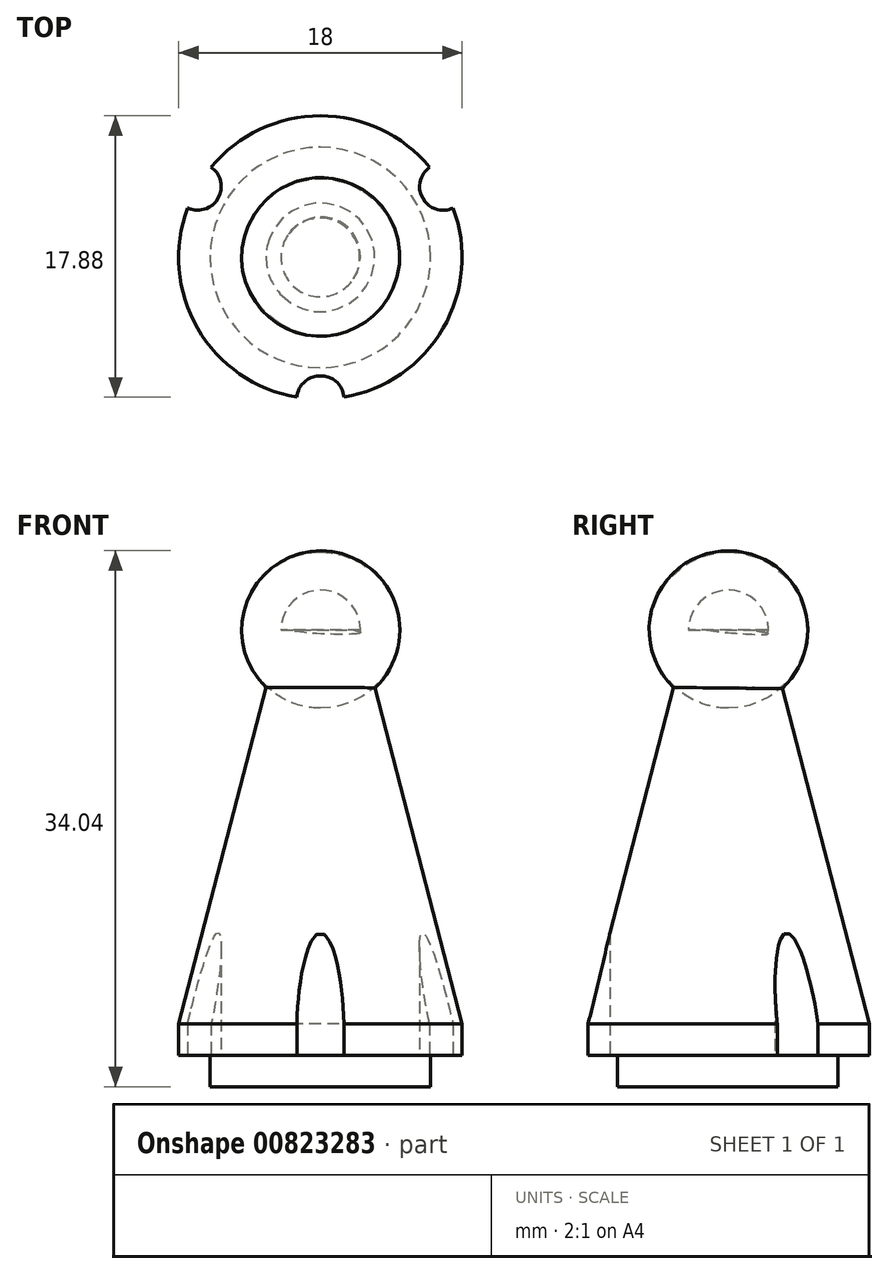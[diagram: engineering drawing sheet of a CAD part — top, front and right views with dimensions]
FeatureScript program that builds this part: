
annotation { "Feature Type Name" : "Feature", "Feature Type Description" : "" }
export const myFeature = defineFeature(function(context is Context, id is Id, definition is map)
    precondition{}
    {
        {
            var Q0;
            Q0=qCreatedBy(makeId("Top.planeOp"),FACE);
            var sketch = newSketch(context, id + "F0", { "sketchPlane" : qUnion([Q0])});
            skCircle(sketch, "E0", {"center": v(0, 0) * mm, "radius": 7 * mm});
            skSolve(sketch);
        }
        {
            var Q0;
            Q0=makeQuery(id+"F0.imprint","IMPRINT",FACE,{"disambiguationData":[TD([[makeQuery(id+"F0.imprint","IMPRINT",EDGE,{"derivedFrom":sQuery(id+"F0.wireOp",EDGE,"E0")}),1.0]])]});
            extrude(context, id + "F1", {"entities" : qUnion([Q0]), "depth" : 2 * mm, "offsetDistance" : 25 * mm});
        }
        {
            var Q0;
            Q0=makeQuery(id+"F1.opExtrude","CAP_FACE",FACE,{"disambiguationData":[OSD([sQuery(id+"F0.wireOp",EDGE,"E0")])],"isStart":false});
            var sketch = newSketch(context, id + "F2", { "sketchPlane" : qUnion([Q0])});
            skCircle(sketch, "E1", {"center": v(0, 0) * mm, "radius": 9 * mm});
            skSolve(sketch);
        }
        {
            var Q0;
            Q0=makeQuery(id+"F2.imprint","IMPRINT",FACE,{"disambiguationData":[TD([[makeQuery(id+"F2.imprint","IMPRINT",EDGE,{"derivedFrom":makeQuery(id+"F1.opExtrude","CAP_EDGE",EDGE,{"disambiguationData":[OSD([sQuery(id+"F0.wireOp",EDGE,"E0")])],"isStart":false})}),1.0]])]});
            var Q1;
            Q1=makeQuery(id+"F2.imprint","IMPRINT",FACE,{"disambiguationData":[TD([[makeQuery(id+"F2.imprint","IMPRINT",EDGE,{"derivedFrom":sQuery(id+"F2.wireOp",EDGE,"E1")}),1.0]])]});
            extrude(context, id + "F3", {"entities" : qUnion([Q0, Q1]), "operationType" : NewBodyOperationType.ADD, "depth" : 2 * mm, "offsetDistance" : 25 * mm});
        }
        {
            var Q0;
            Q0=makeQuery(id+"F3.opExtrude","CAP_FACE",FACE,{"disambiguationData":[OSD([sQuery(id+"F2.wireOp",EDGE,"E1")])],"isStart":false});
            cPlane(context, id + "F4", {"entities" : qUnion([Q0]), "cplaneType" : CPlaneType.OFFSET, "offset" : 25 * mm, "width" : 150 * mm, "height" : 150 * mm});
        }
        {
            var Q0;
            Q0=qCreatedBy(id+"F4.planeOp",FACE);
            var sketch = newSketch(context, id + "F5", { "sketchPlane" : qUnion([Q0])});
            skCircle(sketch, "E2", {"center": v(0, 0) * mm, "radius": 2.5 * mm});
            skSolve(sketch);
        }
        {
            var Q1;
            Q1=makeQuery(id+"F3.opExtrude","CAP_FACE",FACE,{"disambiguationData":[OSD([sQuery(id+"F2.wireOp",EDGE,"E1")])],"isStart":false});
            var Q2;
            Q2=makeQuery(id+"F5.imprint","IMPRINT",FACE,{"disambiguationData":[TD([[makeQuery(id+"F5.imprint","IMPRINT",EDGE,{"derivedFrom":sQuery(id+"F5.wireOp",EDGE,"E2")}),1.0]])]});
            loft(context, id + "F6", {"operationType" : NewBodyOperationType.ADD, "sheetProfilesArray" : [{ "sheetProfileEntities" : qUnion([Q1]) }, { "sheetProfileEntities" : qUnion([Q2]) }]});
        }
        {
            var Q0;
            Q0=makeQuery(id+"F6.opLoft","CAP_FACE",FACE,{"disambiguationData":[OSD([makeQuery(id+"F5.imprint","IMPRINT",FACE,{"disambiguationData":[TD([[makeQuery(id+"F5.imprint","IMPRINT",EDGE,{"derivedFrom":sQuery(id+"F5.wireOp",EDGE,"E2")}),1.0]])]})])],"isStart":true});
            var sketch = newSketch(context, id + "F7", { "sketchPlane" : qUnion([Q0])});
            skCircle(sketch, "E3", {"center": v(0, 0) * mm, "radius": 5 * mm});
            skLineSegment(sketch, "E4", {"start": v(-4.18, 2.74) * mm, "end": v(4.23, -2.67) * mm});
            skSolve(sketch);
        }
        {
            var Q0;
            {var subQ0=sQuery(id+"F7.wireOp",EDGE,"E4");var subQ1=sQuery(id+"F7.wireOp",EDGE,"E3");var subQ2=makeQuery(id+"F7.imprint","INTERSECT",VERTEX,{"disambiguationData":[OD(0.0)],"derivedFrom":[subQ1,subQ0]});Q0=makeQuery(id+"F7.imprint","IMPRINT",FACE,{"disambiguationData":[TD([[makeQuery(id+"F7.imprint","IMPRINT",EDGE,{"disambiguationData":[TD([[subQ2,-1.0]])],"derivedFrom":subQ1}),1.0]])]});}
            var Q1;
            Q1=sQuery(id+"F7.wireOp",EDGE,"E4");
            revolve(context, id + "F8", {"operationType" : NewBodyOperationType.ADD, "surfaceOperationType" : NewSurfaceOperationType.NEW, "entities" : qUnion([Q0]), "axis" : qUnion([Q1]), "revolveType" : RevolveType.FULL});
        }
        {
            var Q0;
            Q0=makeQuery(id+"F3.opExtrude","CAP_FACE",FACE,{"disambiguationData":[OSD([sQuery(id+"F2.wireOp",EDGE,"E1")])],"isStart":true});
            var sketch = newSketch(context, id + "F9", { "sketchPlane" : qUnion([Q0])});
            skCircle(sketch, "E5", {"center": v(0, 9) * mm, "radius": 1.5 * mm});
            skCircle(sketch, "E6.1.0", {"center": v(-7.8, -4.5) * mm, "radius": 1.5 * mm});
            skCircle(sketch, "E6.2.0", {"center": v(7.8, -4.5) * mm, "radius": 1.5 * mm});
            skPoint(sketch, "E6.center", {"position": v(0, 0) * mm});
            skSolve(sketch);
        }
        {
            var Q0;
            {var subQ0=sQuery(id+"F9.wireOp",EDGE,"E6.2.0");var subQ1=makeQuery(id+"F3.opExtrude","CAP_EDGE",EDGE,{"disambiguationData":[OSD([sQuery(id+"F2.wireOp",EDGE,"E1")])],"isStart":true});var subQ2=makeQuery(id+"F9.imprint","INTERSECT",VERTEX,{"disambiguationData":[OD(0.0)],"derivedFrom":[subQ1,subQ0]});Q0=makeQuery(id+"F9.imprint","IMPRINT",FACE,{"disambiguationData":[TD([[makeQuery(id+"F9.imprint","IMPRINT",EDGE,{"disambiguationData":[TD([[subQ2,-1.0]])],"derivedFrom":subQ0}),1.0]])]});}
            var Q1;
            {var subQ0=sQuery(id+"F9.wireOp",EDGE,"E6.1.0");var subQ1=makeQuery(id+"F3.opExtrude","CAP_EDGE",EDGE,{"disambiguationData":[OSD([sQuery(id+"F2.wireOp",EDGE,"E1")])],"isStart":true});var subQ2=makeQuery(id+"F9.imprint","INTERSECT",VERTEX,{"disambiguationData":[OD(0.0)],"derivedFrom":[subQ1,subQ0]});Q1=makeQuery(id+"F9.imprint","IMPRINT",FACE,{"disambiguationData":[TD([[makeQuery(id+"F9.imprint","IMPRINT",EDGE,{"disambiguationData":[TD([[subQ2,-1.0]])],"derivedFrom":subQ0}),1.0]])]});}
            var Q2;
            {var subQ0=sQuery(id+"F9.wireOp",EDGE,"E5");var subQ1=makeQuery(id+"F3.opExtrude","CAP_EDGE",EDGE,{"disambiguationData":[OSD([sQuery(id+"F2.wireOp",EDGE,"E1")])],"isStart":true});var subQ2=makeQuery(id+"F9.imprint","INTERSECT",VERTEX,{"disambiguationData":[OD(0.0)],"derivedFrom":[subQ1,subQ0]});Q2=makeQuery(id+"F9.imprint","IMPRINT",FACE,{"disambiguationData":[TD([[makeQuery(id+"F9.imprint","IMPRINT",EDGE,{"disambiguationData":[TD([[subQ2,1.0]])],"derivedFrom":subQ0}),1.0]])]});}
            var Q3;
            {var subQ0=sQuery(id+"F9.wireOp",EDGE,"E6.2.0");var subQ1=makeQuery(id+"F3.opExtrude","CAP_EDGE",EDGE,{"disambiguationData":[OSD([sQuery(id+"F2.wireOp",EDGE,"E1")])],"isStart":true});var subQ2=makeQuery(id+"F9.imprint","INTERSECT",VERTEX,{"disambiguationData":[OD(0.0)],"derivedFrom":[subQ1,subQ0]});Q3=makeQuery(id+"F9.imprint","IMPRINT",FACE,{"disambiguationData":[TD([[makeQuery(id+"F9.imprint","IMPRINT",EDGE,{"disambiguationData":[TD([[subQ2,1.0]])],"derivedFrom":subQ0}),1.0]])]});}
            var Q4;
            {var subQ0=sQuery(id+"F9.wireOp",EDGE,"E5");var subQ1=makeQuery(id+"F3.opExtrude","CAP_EDGE",EDGE,{"disambiguationData":[OSD([sQuery(id+"F2.wireOp",EDGE,"E1")])],"isStart":true});var subQ2=makeQuery(id+"F9.imprint","INTERSECT",VERTEX,{"disambiguationData":[OD(0.0)],"derivedFrom":[subQ1,subQ0]});Q4=makeQuery(id+"F9.imprint","IMPRINT",FACE,{"disambiguationData":[TD([[makeQuery(id+"F9.imprint","IMPRINT",EDGE,{"disambiguationData":[TD([[subQ2,-1.0]])],"derivedFrom":subQ0}),1.0]])]});}
            var Q5;
            {var subQ0=sQuery(id+"F9.wireOp",EDGE,"E6.1.0");var subQ1=makeQuery(id+"F3.opExtrude","CAP_EDGE",EDGE,{"disambiguationData":[OSD([sQuery(id+"F2.wireOp",EDGE,"E1")])],"isStart":true});var subQ2=makeQuery(id+"F9.imprint","INTERSECT",VERTEX,{"disambiguationData":[OD(0.0)],"derivedFrom":[subQ1,subQ0]});Q5=makeQuery(id+"F9.imprint","IMPRINT",FACE,{"disambiguationData":[TD([[makeQuery(id+"F9.imprint","IMPRINT",EDGE,{"disambiguationData":[TD([[subQ2,1.0]])],"derivedFrom":subQ0}),1.0]])]});}
            extrude(context, id + "F10", {"entities" : qUnion([Q0, Q1, Q2, Q3, Q4, Q5]), "operationType" : NewBodyOperationType.REMOVE, "endBound" : BoundingType.THROUGH_ALL, "oppositeDirection" : true, "depth" : 2 * mm, "offsetDistance" : 25 * mm});
        }
    });
